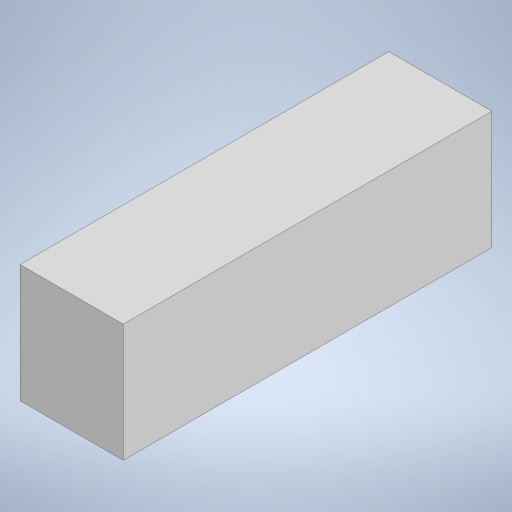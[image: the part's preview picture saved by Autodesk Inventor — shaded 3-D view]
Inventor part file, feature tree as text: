
AUTODESK INVENTOR PART (.ipt)
format: ipt  version: 2024 (Build 280153000, 153)  size: 176,640 bytes
history: native  units: mm
features: extrude x1, sketch x1
ambient origin geometry x8: Origin, YZ Plane, XZ Plane, XY Plane, X Axis, Y Axis, Z Axis, Center Point
bodies: Solid1 (feature_tree)
feature tree (2):
  extrude  "Extrusion1"  Depth=8.0mm
  sketch  "Sketch1"  dims[d0=7.0mm d1=8.0mm d2=25.0mm d3=0.0mm]
